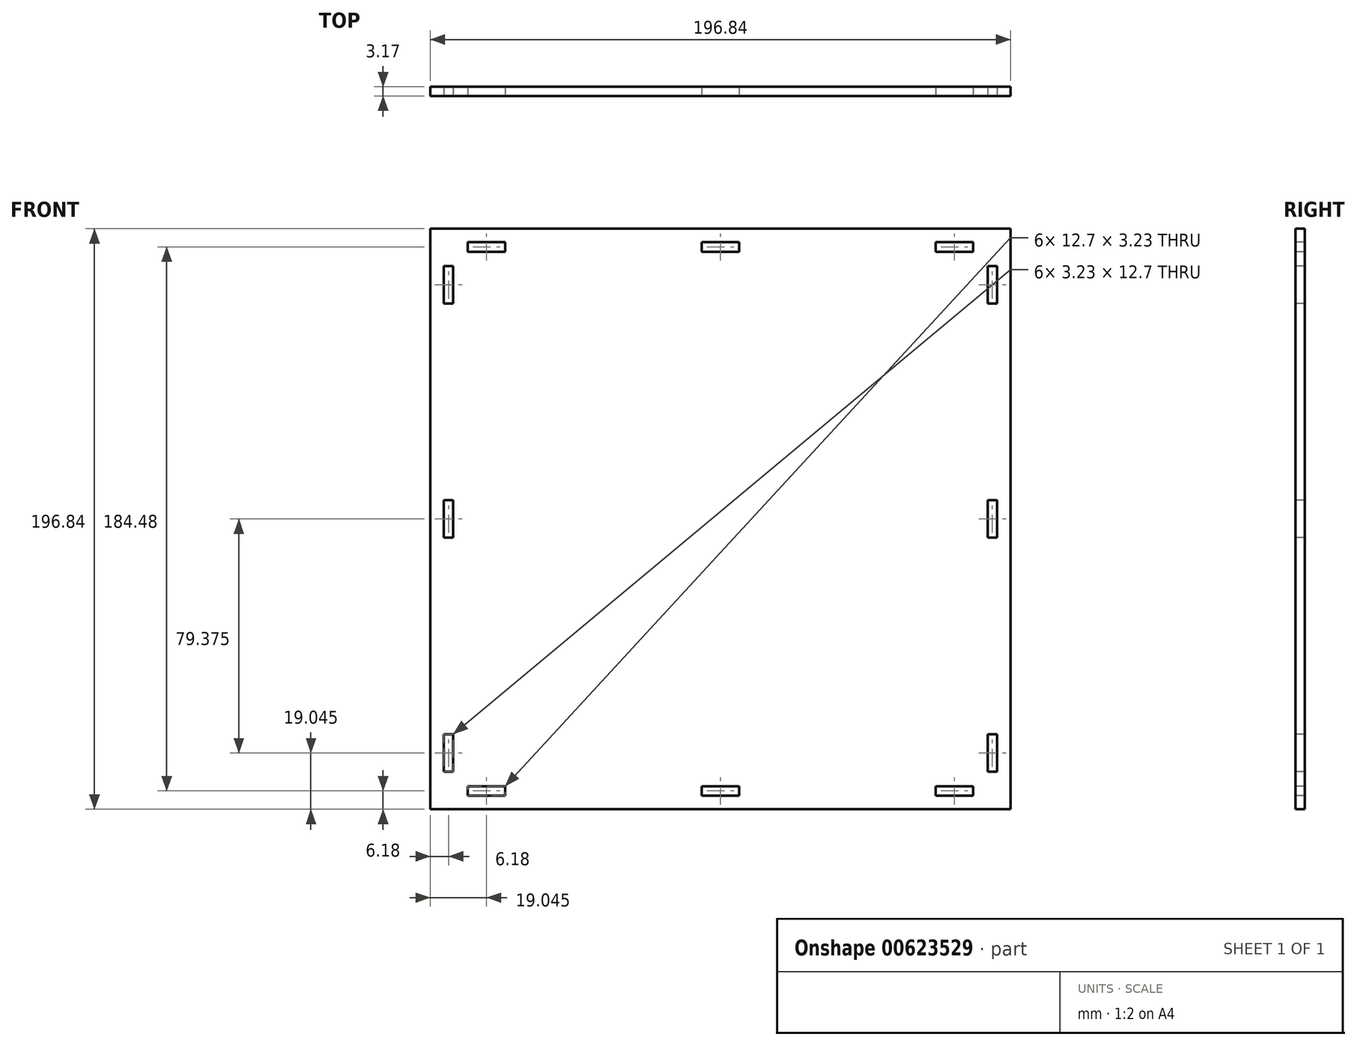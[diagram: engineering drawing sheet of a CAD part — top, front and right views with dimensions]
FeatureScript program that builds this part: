
annotation { "Feature Type Name" : "Feature", "Feature Type Description" : "" }
export const myFeature = defineFeature(function(context is Context, id is Id, definition is map)
    precondition{}
    {
        {
            var Q0;
            Q0=qCreatedBy(makeId("Front.planeOp"),FACE);
            var sketch = newSketch(context, id + "F0", { "sketchPlane" : qUnion([Q0])});
            skLineSegment(sketch, "E0.bottom", {"start": v(98.43, -98.42) * mm, "end": v(-98.43, -98.42) * mm});
            skLineSegment(sketch, "E0.top", {"start": v(98.42, 98.42) * mm, "end": v(-98.43, 98.42) * mm});
            skLineSegment(sketch, "E0.left", {"start": v(98.43, -98.42) * mm, "end": v(98.42, 98.43) * mm});
            skLineSegment(sketch, "E0.right", {"start": v(-98.42, -98.42) * mm, "end": v(-98.43, 98.43) * mm});
            skPoint(sketch, "E0.middle", {"position": v(0, 0) * mm});
            skSolve(sketch);
        }
        {
            var Q0;
            Q0 = qSketchRegion(id + "F0", true);
            extrude(context, id + "F1", {"entities" : qUnion([Q0]), "depth" : 3.17 * mm, "offsetDistance" : 25.4 * mm});
        }
        {
            var Q0;
            Q0=makeQuery(id+"F1.opExtrude","CAP_FACE",FACE,{"disambiguationData":[OSD([sQuery(id+"F0.wireOp",EDGE,"E0.bottom"),sQuery(id+"F0.wireOp",EDGE,"E0.top"),sQuery(id+"F0.wireOp",EDGE,"E0.left"),sQuery(id+"F0.wireOp",EDGE,"E0.right")])],"isStart":false});
            var sketch = newSketch(context, id + "F2", { "sketchPlane" : qUnion([Q0])});
            skLineSegment(sketch, "E1.bottom", {"start": v(85.73, -90.63) * mm, "end": v(85.73, -93.85) * mm});
            skLineSegment(sketch, "E1.top", {"start": v(73.03, -90.63) * mm, "end": v(73.03, -93.85) * mm});
            skLineSegment(sketch, "E1.left", {"start": v(85.73, -90.63) * mm, "end": v(73.03, -90.63) * mm});
            skLineSegment(sketch, "E1.right", {"start": v(85.73, -93.85) * mm, "end": v(73.03, -93.85) * mm});
            skLineSegment(sketch, "E2.MirrorCS", {"start": v(93.85, 85.73) * mm, "end": v(93.85, 73.03) * mm});
            skLineSegment(sketch, "E3.MirrorCS", {"start": v(93.85, 73.03) * mm, "end": v(90.63, 73.03) * mm});
            skLineSegment(sketch, "E4.MirrorCS", {"start": v(90.63, 85.73) * mm, "end": v(90.63, 73.03) * mm});
            skLineSegment(sketch, "E5.MirrorCS", {"start": v(93.85, -73.02) * mm, "end": v(90.63, -73.02) * mm});
            skLineSegment(sketch, "E6.MirrorCS", {"start": v(93.85, -85.72) * mm, "end": v(90.63, -85.72) * mm});
            skLineSegment(sketch, "E7.MirrorCS", {"start": v(93.85, 85.73) * mm, "end": v(90.63, 85.73) * mm});
            skLineSegment(sketch, "E8.MirrorCS", {"start": v(93.85, -85.72) * mm, "end": v(93.85, -73.02) * mm});
            skLineSegment(sketch, "E9.MirrorCS", {"start": v(90.63, -85.72) * mm, "end": v(90.63, -73.02) * mm});
            skLineSegment(sketch, "E10.bottom", {"start": v(6.35, -90.63) * mm, "end": v(6.35, -93.85) * mm});
            skLineSegment(sketch, "E10.top", {"start": v(-6.35, -90.63) * mm, "end": v(-6.35, -93.85) * mm});
            skLineSegment(sketch, "E10.left", {"start": v(6.35, -90.63) * mm, "end": v(-6.35, -90.63) * mm});
            skLineSegment(sketch, "E10.right", {"start": v(6.35, -93.85) * mm, "end": v(-6.35, -93.85) * mm});
            skLineSegment(sketch, "E11.MirrorCS", {"start": v(93.85, 6.35) * mm, "end": v(90.63, 6.35) * mm});
            skLineSegment(sketch, "E12.MirrorCS", {"start": v(93.85, -6.35) * mm, "end": v(90.63, -6.35) * mm});
            skLineSegment(sketch, "E13.MirrorCS", {"start": v(93.85, 6.35) * mm, "end": v(93.85, -6.35) * mm});
            skLineSegment(sketch, "E14.MirrorCS", {"start": v(90.63, 6.35) * mm, "end": v(90.63, -6.35) * mm});
            skLineSegment(sketch, "E15.MirrorCS", {"start": v(-85.73, -90.63) * mm, "end": v(-85.73, -93.85) * mm});
            skLineSegment(sketch, "E16.MirrorCS", {"start": v(-85.73, -93.85) * mm, "end": v(-73.03, -93.85) * mm});
            skLineSegment(sketch, "E17.MirrorCS", {"start": v(-85.73, -90.63) * mm, "end": v(-73.03, -90.63) * mm});
            skLineSegment(sketch, "E18.MirrorCS", {"start": v(-73.03, -90.63) * mm, "end": v(-73.03, -93.85) * mm});
            skLineSegment(sketch, "E19.MirrorCS", {"start": v(-93.85, 73.02) * mm, "end": v(-90.63, 73.02) * mm});
            skLineSegment(sketch, "E20.MirrorCS", {"start": v(-93.85, 85.72) * mm, "end": v(-90.63, 85.72) * mm});
            skLineSegment(sketch, "E21.MirrorCS", {"start": v(-93.85, -85.72) * mm, "end": v(-90.63, -85.72) * mm});
            skLineSegment(sketch, "E22.MirrorCS", {"start": v(-93.85, -6.35) * mm, "end": v(-90.63, -6.35) * mm});
            skLineSegment(sketch, "E23.MirrorCS", {"start": v(-93.85, 6.35) * mm, "end": v(-90.63, 6.35) * mm});
            skLineSegment(sketch, "E24.MirrorCS", {"start": v(-93.85, -73.02) * mm, "end": v(-90.63, -73.02) * mm});
            skLineSegment(sketch, "E25.MirrorCS", {"start": v(-90.63, 85.72) * mm, "end": v(-90.63, 73.02) * mm});
            skLineSegment(sketch, "E26.MirrorCS", {"start": v(-93.85, 85.72) * mm, "end": v(-93.85, 73.02) * mm});
            skLineSegment(sketch, "E27.MirrorCS", {"start": v(-93.85, -85.72) * mm, "end": v(-93.85, -73.02) * mm});
            skLineSegment(sketch, "E28.MirrorCS", {"start": v(-90.63, -85.72) * mm, "end": v(-90.63, -73.02) * mm});
            skLineSegment(sketch, "E29.MirrorCS", {"start": v(-90.63, 6.35) * mm, "end": v(-90.63, -6.35) * mm});
            skLineSegment(sketch, "E30.MirrorCS", {"start": v(-93.85, 6.35) * mm, "end": v(-93.85, -6.35) * mm});
            skLineSegment(sketch, "E31.MirrorCS", {"start": v(-85.73, 90.63) * mm, "end": v(-85.73, 93.85) * mm});
            skLineSegment(sketch, "E32.MirrorCS", {"start": v(-6.35, 90.63) * mm, "end": v(-6.35, 93.85) * mm});
            skLineSegment(sketch, "E33.MirrorCS", {"start": v(-73.03, 90.63) * mm, "end": v(-73.03, 93.85) * mm});
            skLineSegment(sketch, "E34.MirrorCS", {"start": v(73.03, 90.63) * mm, "end": v(73.03, 93.85) * mm});
            skLineSegment(sketch, "E35.MirrorCS", {"start": v(85.73, 90.63) * mm, "end": v(85.73, 93.85) * mm});
            skLineSegment(sketch, "E36.MirrorCS", {"start": v(6.35, 90.63) * mm, "end": v(6.35, 93.85) * mm});
            skLineSegment(sketch, "E37.MirrorCS", {"start": v(-85.73, 93.85) * mm, "end": v(-73.03, 93.85) * mm});
            skLineSegment(sketch, "E38.MirrorCS", {"start": v(6.35, 93.85) * mm, "end": v(-6.35, 93.85) * mm});
            skLineSegment(sketch, "E39.MirrorCS", {"start": v(6.35, 90.63) * mm, "end": v(-6.35, 90.63) * mm});
            skLineSegment(sketch, "E40.MirrorCS", {"start": v(-85.73, 90.63) * mm, "end": v(-73.03, 90.63) * mm});
            skLineSegment(sketch, "E41.MirrorCS", {"start": v(85.73, 93.85) * mm, "end": v(73.03, 93.85) * mm});
            skLineSegment(sketch, "E42.MirrorCS", {"start": v(85.73, 90.63) * mm, "end": v(73.03, 90.63) * mm});
            skSolve(sketch);
        }
        {
            var Q0;
            Q0 = qSketchRegion(id + "F2", true);
            extrude(context, id + "F3", {"entities" : qUnion([Q0]), "operationType" : NewBodyOperationType.REMOVE, "oppositeDirection" : true, "depth" : 3.17 * mm, "offsetDistance" : 25.4 * mm});
        }
    });
